# Revit family: Paneles planos de interconexión cobre
name_source: partatom
category: Equipement spécialisé
units: mm (PartAtom-declared; Revit-internal decimal feet)

## family parameters
Basée sur le plan de construction = Non
Cote de connecteur circulaire = Utiliser le diamètre
Couper avec des vides une fois chargée = Non
Partagée = Oui
Point de calcul de pièce = Non
Toujours verticalement = Oui
Type d'élément = Normal

## types (8) — shared parameters
Clase de aplicación = EC001128
Clase de protección IK = IK03
Color = IDS_NOIR
E-catalogo enlace = https://www.legrand.fr
Función = Paneles de interconexión planos y equipados
Módulos de altura = 1
Natura del cable para la conexión = Flexible o rígido
Numero RAL = 9017
Número de conectores = 24
Soporte del cable = En zigzag
Tamaño modular = 19 pulgadas
Temperatura de almacenamiento = -40°C à 70°C
Temperatura operativa = -25°C à 70°C
Tipo de conector = RJ45
Tipo de conexión = Toma vampiro para cable plano
zero-valued in all types: Elévation par défaut

## per-type parameters (varying)
| type | Altura | Anchura (mm) | Blindado | Categoria | EAN | Número de pieza Legrand | Profundidad |
| Panel de interconexión plano 24 RJ45 Cat 5e UTP 1U | 43.85 mm  [stored 0.143865 ft] | 482.5 mm | Non | 5E | 3414970870308 | 033750 | 321.7 mm |
| Panel de interconexión plano 24 RJ45 Cat 5e FTP 1U | 43.85 mm  [stored 0.143865 ft] | 482.5 mm | Oui | 5E | 3414970870322 | 033751 | 321.7 mm |
| Panel de interconexión plano 24 RJ45 Cat 6 UTP 1U | 43.85 mm  [stored 0.143865 ft] | 482.5 mm | Non | 6 | 3414970870537 | 033760 | 321.7 mm |
| Panel de interconexión plano 24 RJ45 Cat 6 FTP 1U | 43.85 mm  [stored 0.143865 ft] | 482.5 mm | Oui | 6 | 3414970870551 | 033761 | 321.7 mm |
| Panel de interconexión plano 24 RJ45 Cat 6 STP 1U | 43.85 mm  [stored 0.143865 ft] | 482.5 mm | Oui | 6 | 3414970870575 | 033762 | 321.7 mm |
| Panel de interconexión plano 24 RJ45 Cat 6A UTP 1U | 43.85 mm  [stored 0.143865 ft] | 482.5 mm | Non | 6A | 3414970870681 | 033770 | 321.7 mm |
| Panel de interconexión plano 24 RJ45 Cat 6A STP 1U | 43.85 mm  [stored 0.143865 ft] | 482.5 mm | Oui | 6A | 3414970870704 | 033772 | 321.7 mm |
| Panel de interconexión plano 24 RJ45 Cat 8 STP 1U | 44.45 mm | 482.6 mm | Oui | 8 | 3414970982063 | 033782 | 120 mm |

note: column(s) folded — value = type name in every type: Formulación BIM

note: [stored X ft] marks values corroborated as IEEE doubles in the binary element streams (Revit-internal decimal feet)
